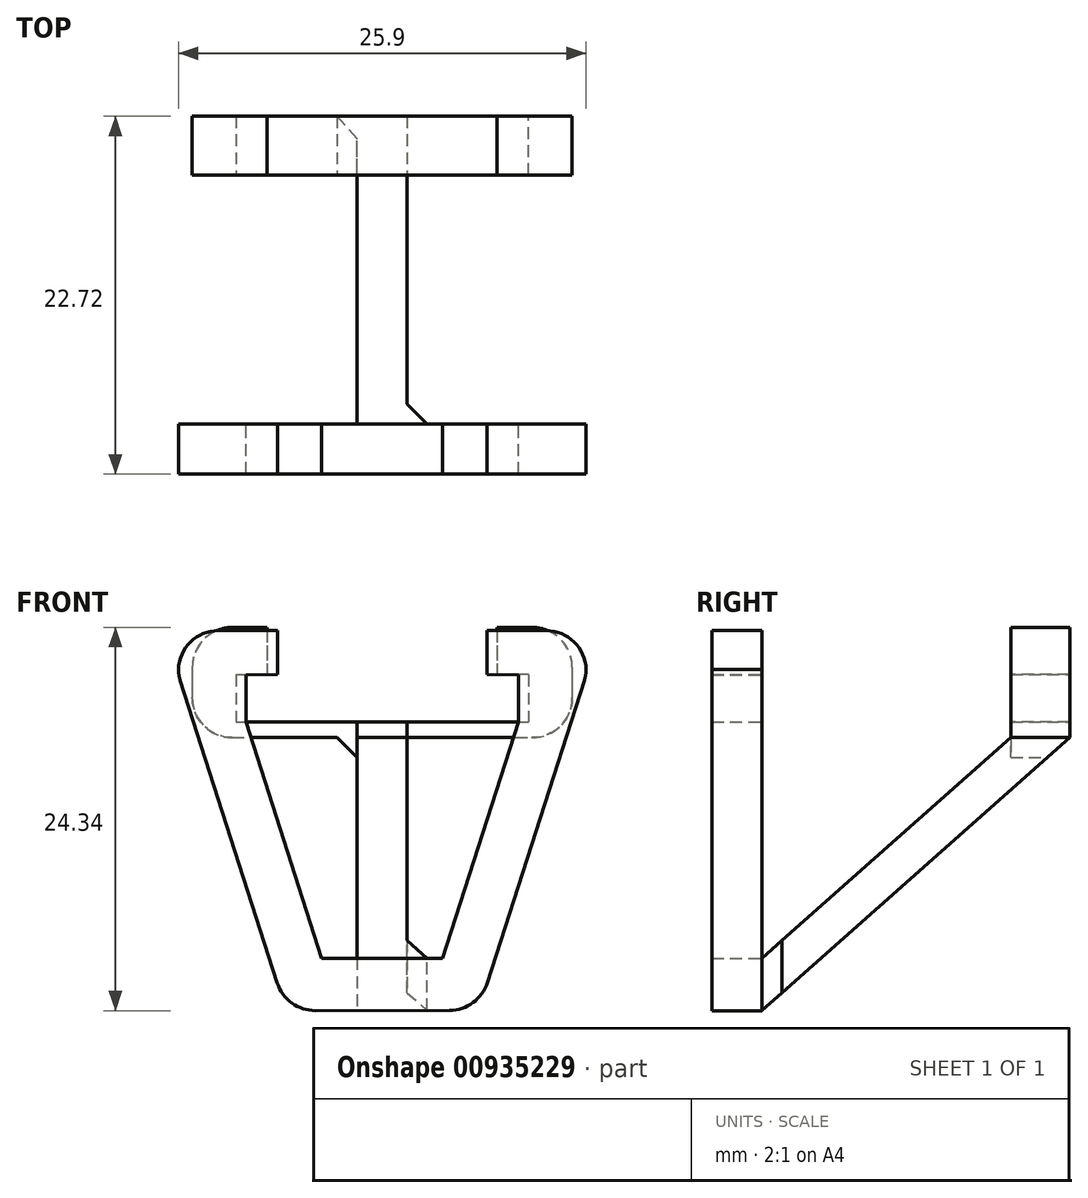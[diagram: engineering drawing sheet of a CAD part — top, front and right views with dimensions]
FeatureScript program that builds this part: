
annotation { "Feature Type Name" : "Feature", "Feature Type Description" : "" }
export const myFeature = defineFeature(function(context is Context, id is Id, definition is map)
    precondition{}
    {
        {
            var Q0;
            Q0=qCreatedBy(makeId("Front.planeOp"),FACE);
            var sketch = newSketch(context, id + "F0", { "sketchPlane" : qUnion([Q0])});
            skLineSegment(sketch, "E0", {"start": v(-3.84, -7.5) * mm, "end": v(3.84, -7.5) * mm});
            skLineSegment(sketch, "E1", {"start": v(3.84, -7.5) * mm, "end": v(8.65, 7.5) * mm});
            skLineSegment(sketch, "E2", {"start": v(8.65, 7.5) * mm, "end": v(-8.65, 7.5) * mm, "construction": true});
            skLineSegment(sketch, "E3", {"start": v(-8.65, 7.5) * mm, "end": v(-3.84, -7.5) * mm});
            skPoint(sketch, "E4", {"position": v(0, 7.5) * mm});
            skPoint(sketch, "E5", {"position": v(0, -7.5) * mm});
            skPoint(sketch, "E6", {"position": v(-6.24, 0) * mm});
            skPoint(sketch, "E7", {"position": v(6.24, 0) * mm});
            skLineSegment(sketch, "E8.1", {"start": v(6.12, -10.8) * mm, "end": v(12.96, 10.55) * mm});
            skLineSegment(sketch, "E8.2", {"start": v(-6.1, -10.83) * mm, "end": v(6.12, -10.8) * mm});
            skLineSegment(sketch, "E8.3", {"start": v(-12.95, 10.51) * mm, "end": v(-6.1, -10.83) * mm});
            skLineSegment(sketch, "E9", {"start": v(-8.65, 7.5) * mm, "end": v(-8.65, 10.5) * mm});
            skLineSegment(sketch, "E10", {"start": v(8.65, 7.5) * mm, "end": v(8.65, 10.5) * mm});
            skLineSegment(sketch, "E11", {"start": v(-12.95, 10.51) * mm, "end": v(-12.95, 13.3) * mm});
            skLineSegment(sketch, "E12", {"start": v(-12.95, 13.3) * mm, "end": v(-6.65, 13.3) * mm});
            skLineSegment(sketch, "E13", {"start": v(-6.65, 13.3) * mm, "end": v(-6.65, 10.51) * mm});
            skLineSegment(sketch, "E14", {"start": v(-6.65, 10.51) * mm, "end": v(-8.65, 10.5) * mm});
            skLineSegment(sketch, "E15", {"start": v(0, 0) * mm, "end": v(0, 10.33) * mm, "construction": true});
            skLineSegment(sketch, "E16.MirrorCS", {"start": v(6.65, 13.3) * mm, "end": v(6.65, 10.51) * mm});
            skLineSegment(sketch, "E17.MirrorCS", {"start": v(12.95, 13.3) * mm, "end": v(6.65, 13.3) * mm});
            skLineSegment(sketch, "E18.MirrorCS", {"start": v(12.95, 10.51) * mm, "end": v(12.95, 13.3) * mm});
            skLineSegment(sketch, "E19", {"start": v(6.65, 10.51) * mm, "end": v(8.65, 10.5) * mm});
            skSolve(sketch);
        }
        {
            var Q0;
            Q0 = qSketchRegion(id + "F0", true);
            extrude(context, id + "F1", {"entities" : qUnion([Q0]), "depth" : 3.17 * mm, "offsetDistance" : 25.4 * mm});
        }
        {
            var Q0;
            Q0=qCreatedBy(makeId("Right.planeOp"),FACE);
            var sketch = newSketch(context, id + "F2", { "sketchPlane" : qUnion([Q0])});
            skLineSegment(sketch, "E20", {"start": v(0, -10.82) * mm, "end": v(19.55, 6.51) * mm});
            skLineSegment(sketch, "E21", {"start": v(19.55, 6.51) * mm, "end": v(15.8, 6.51) * mm});
            skLineSegment(sketch, "E22", {"start": v(15.8, 6.51) * mm, "end": v(0, -7.5) * mm});
            skLineSegment(sketch, "E23", {"start": v(0, -7.5) * mm, "end": v(0, -10.82) * mm});
            skLineSegment(sketch, "E24", {"start": v(9.63, 10.51) * mm, "end": v(-11.69, 10.51) * mm, "construction": true});
            skSolve(sketch);
        }
        {
            var Q0;
            Q0 = qSketchRegion(id + "F2", true);
            extrude(context, id + "F3", {"entities" : qUnion([Q0]), "operationType" : NewBodyOperationType.ADD, "depth" : 1.59 * mm, "offsetDistance" : 25.4 * mm, "hasSecondDirection" : true, "secondDirectionOppositeDirection" : true, "secondDirectionDepth" : 1.59 * mm});
        }
        {
            var Q0;
            Q0=makeQuery(id+"F3.opExtrude","SWEPT_FACE",FACE,{"disambiguationData":[OSD([sQuery(id+"F2.wireOp",EDGE,"E21")])]});
            var sketch = newSketch(context, id + "F4", { "sketchPlane" : qUnion([Q0])});
            skLineSegment(sketch, "E25", {"start": v(-12.07, 19.55) * mm, "end": v(12.07, 19.55) * mm});
            skLineSegment(sketch, "E26", {"start": v(12.06, 19.55) * mm, "end": v(12.07, 15.81) * mm});
            skLineSegment(sketch, "E27", {"start": v(-12.06, 15.81) * mm, "end": v(-12.07, 19.55) * mm});
            skPoint(sketch, "E28", {"position": v(0, 19.55) * mm});
            skLineSegment(sketch, "E29", {"start": v(-12.06, 15.81) * mm, "end": v(12.06, 15.81) * mm});
            skSolve(sketch);
        }
        {
            var Q0;
            {var subQ2=sQuery(id+"F4.wireOp",EDGE,"E27");Q0=makeQuery(id+"F4.imprint","IMPRINT",FACE,{"disambiguationData":[TD([[makeQuery(id+"F4.imprint","IMPRINT",EDGE,{"derivedFrom":subQ2}),-1.0]])]});}
            var Q1;
            {var subQ2=sQuery(id+"F4.wireOp",EDGE,"E26");Q1=makeQuery(id+"F4.imprint","IMPRINT",FACE,{"disambiguationData":[TD([[makeQuery(id+"F4.imprint","IMPRINT",EDGE,{"derivedFrom":subQ2}),-1.0]])]});}
            var Q2;
            {var subQ1=sQuery(id+"F2.wireOp",EDGE,"E21");var subQ2=makeQuery(id+"F3.opExtrude","CAP_EDGE",EDGE,{"disambiguationData":[OSD([subQ1])],"isStart":true});Q2=makeQuery(id+"F4.imprint","IMPRINT",FACE,{"disambiguationData":[TD([[makeQuery(id+"F4.imprint","IMPRINT",EDGE,{"derivedFrom":subQ2}),1.0]])]});}
            extrude(context, id + "F5", {"entities" : qUnion([Q0, Q1, Q2]), "operationType" : NewBodyOperationType.ADD, "surfaceOperationType" : NewSurfaceOperationType.ADD, "depth" : 1 * mm, "offsetDistance" : 25.4 * mm});
        }
        {
            var Q0;
            Q0=makeQuery(id+"F5.opExtrude","CAP_FACE",FACE,{"disambiguationData":[OSD([sQuery(id+"F4.wireOp",EDGE,"E25"),sQuery(id+"F4.wireOp",EDGE,"E26"),sQuery(id+"F4.wireOp",EDGE,"JMsBaGrd-YBFe-lk9z-cFID-vuqrFTMM80rK"),sQuery(id+"F4.wireOp",EDGE,"E27")])],"isStart":false});
            var sketch = newSketch(context, id + "F6", { "sketchPlane" : qUnion([Q0])});
            skLineSegment(sketch, "E30", {"start": v(-12.07, 19.55) * mm, "end": v(-9.3, 19.55) * mm});
            skLineSegment(sketch, "E31", {"start": v(9.3, 19.55) * mm, "end": v(12.07, 19.55) * mm});
            skLineSegment(sketch, "E32", {"start": v(-9.3, 19.55) * mm, "end": v(-9.3, 15.81) * mm});
            skLineSegment(sketch, "E33", {"start": v(-12.06, 15.81) * mm, "end": v(-12.07, 19.55) * mm});
            skLineSegment(sketch, "E34", {"start": v(12.07, 15.81) * mm, "end": v(12.07, 19.55) * mm});
            skLineSegment(sketch, "E35", {"start": v(9.3, 15.81) * mm, "end": v(12.07, 15.81) * mm});
            skLineSegment(sketch, "E36", {"start": v(9.3, 15.81) * mm, "end": v(9.3, 19.55) * mm});
            skLineSegment(sketch, "E37", {"start": v(-9.3, 15.81) * mm, "end": v(-12.06, 15.81) * mm});
            skSolve(sketch);
        }
        {
            var Q0;
            Q0 = qSketchRegion(id + "F6", true);
            extrude(context, id + "F7", {"entities" : qUnion([Q0]), "operationType" : NewBodyOperationType.ADD, "depth" : 3 * mm, "offsetDistance" : 25.4 * mm});
        }
        {
            var Q0;
            Q0=makeQuery(id+"F7.opExtrude","CAP_FACE",FACE,{"disambiguationData":[OSD([sQuery(id+"F6.wireOp",EDGE,"FQHeRqek-PSTe-Z9Ou-YJmQ-FMx1T6HD9IbX"),sQuery(id+"F6.wireOp",EDGE,"EPg83Q0q-uvmD-hmRD-8swU-ACq6v45OFrNL"),sQuery(id+"F6.wireOp",EDGE,"iW2Um3Yn-hzmQ-3CLZ-odkE-eqQZqS0yNJDa"),sQuery(id+"F6.wireOp",EDGE,"E30")])],"isStart":false});
            var sketch = newSketch(context, id + "F8", { "sketchPlane" : qUnion([Q0])});
            skLineSegment(sketch, "E38.bottom", {"start": v(-12.07, 19.55) * mm, "end": v(-7.3, 19.55) * mm});
            skLineSegment(sketch, "E38.top", {"start": v(-12.06, 15.81) * mm, "end": v(-7.3, 15.81) * mm});
            skLineSegment(sketch, "E38.left", {"start": v(-12.07, 15.81) * mm, "end": v(-12.07, 19.55) * mm});
            skLineSegment(sketch, "E38.right", {"start": v(-7.3, 15.81) * mm, "end": v(-7.3, 19.55) * mm});
            skLineSegment(sketch, "E39.bottom", {"start": v(12.07, 19.55) * mm, "end": v(7.3, 19.55) * mm});
            skLineSegment(sketch, "E39.top", {"start": v(12.07, 15.81) * mm, "end": v(7.3, 15.81) * mm});
            skLineSegment(sketch, "E39.left", {"start": v(12.07, 15.81) * mm, "end": v(12.07, 19.55) * mm});
            skLineSegment(sketch, "E39.right", {"start": v(7.3, 15.81) * mm, "end": v(7.3, 19.55) * mm});
            skSolve(sketch);
        }
        {
            var Q0;
            Q0 = qSketchRegion(id + "F8", true);
            extrude(context, id + "F9", {"entities" : qUnion([Q0]), "operationType" : NewBodyOperationType.ADD, "depth" : 3 * mm, "offsetDistance" : 25.4 * mm});
        }
        {
            var Q0;
            Q0=makeQuery(id+"F3.opExtrude","CAP_EDGE",EDGE,{"disambiguationData":[OSD([sQuery(id+"F2.wireOp",EDGE,"E21")])],"isStart":false});
            var Q1;
            Q1=makeQuery(id+"F3.opExtrude","CAP_EDGE",EDGE,{"disambiguationData":[OSD([sQuery(id+"F2.wireOp",EDGE,"E21")])],"isStart":true});
            var Q2;
            Q2=makeQuery(id+"F3.opExtrude","CAP_EDGE",EDGE,{"disambiguationData":[OSD([sQuery(id+"F2.wireOp",EDGE,"E23")])],"isStart":false});
            var Q3;
            Q3=makeQuery(id+"F3.opExtrude","CAP_EDGE",EDGE,{"disambiguationData":[OSD([sQuery(id+"F2.wireOp",EDGE,"E23")])],"isStart":true});
            chamfer(context, id + "F10", {"entities" : qUnion([Q0, Q1, Q2, Q3]), "width" : 1.27 * mm, "tangentPropagation" : true});
        }
        {
            var Q0;
            Q0=makeQuery(id+"F5.opExtrude","CAP_EDGE",EDGE,{"disambiguationData":[OSD([sQuery(id+"F4.wireOp",EDGE,"E27")])],"isStart":true});
            var Q1;
            Q1=makeQuery(id+"F5.opExtrude","CAP_EDGE",EDGE,{"disambiguationData":[OSD([sQuery(id+"F4.wireOp",EDGE,"E26")])],"isStart":true});
            var Q2;
            Q2=makeQuery(id+"F9.opExtrude","CAP_EDGE",EDGE,{"disambiguationData":[OSD([sQuery(id+"F8.wireOp",EDGE,"E39.left")])],"isStart":false});
            var Q3;
            Q3=makeQuery(id+"F9.opExtrude","CAP_EDGE",EDGE,{"disambiguationData":[OSD([sQuery(id+"F8.wireOp",EDGE,"E38.left")])],"isStart":false});
            var Q4;
            Q4=makeQuery(id+"F1.opExtrude","SWEPT_EDGE",EDGE,{"disambiguationData":[OSD([sQuery(id+"F0.wireOp",EDGE,"E11"),sQuery(id+"F0.wireOp",EDGE,"E12")])]});
            var Q5;
            Q5=makeQuery(id+"F1.opExtrude","SWEPT_EDGE",EDGE,{"disambiguationData":[OSD([sQuery(id+"F0.wireOp",EDGE,"E8.3"),sQuery(id+"F0.wireOp",EDGE,"E11")])]});
            var Q6;
            Q6=makeQuery(id+"F1.opExtrude","SWEPT_EDGE",EDGE,{"disambiguationData":[OSD([sQuery(id+"F0.wireOp",EDGE,"E17.MirrorCS"),sQuery(id+"F0.wireOp",EDGE,"E18.MirrorCS")])]});
            var Q7;
            Q7=makeQuery(id+"F1.opExtrude","SWEPT_EDGE",EDGE,{"disambiguationData":[OSD([sQuery(id+"F0.wireOp",EDGE,"E8.1"),sQuery(id+"F0.wireOp",EDGE,"E18.MirrorCS")])]});
            var Q8;
            Q8=makeQuery(id+"F1.opExtrude","SWEPT_EDGE",EDGE,{"disambiguationData":[OSD([sQuery(id+"F0.wireOp",EDGE,"E8.1"),sQuery(id+"F0.wireOp",EDGE,"E8.2")])]});
            var Q9;
            Q9=makeQuery(id+"F1.opExtrude","SWEPT_EDGE",EDGE,{"disambiguationData":[OSD([sQuery(id+"F0.wireOp",EDGE,"E8.2"),sQuery(id+"F0.wireOp",EDGE,"E8.3")])]});
            fillet(context, id + "F11", {"entities" : qUnion([Q0, Q1, Q2, Q3, Q4, Q5, Q6, Q7, Q8, Q9]), "radius" : 2.54 * mm, "tangentPropagation" : true, "allowEdgeOverflow" : false});
        }
    });
